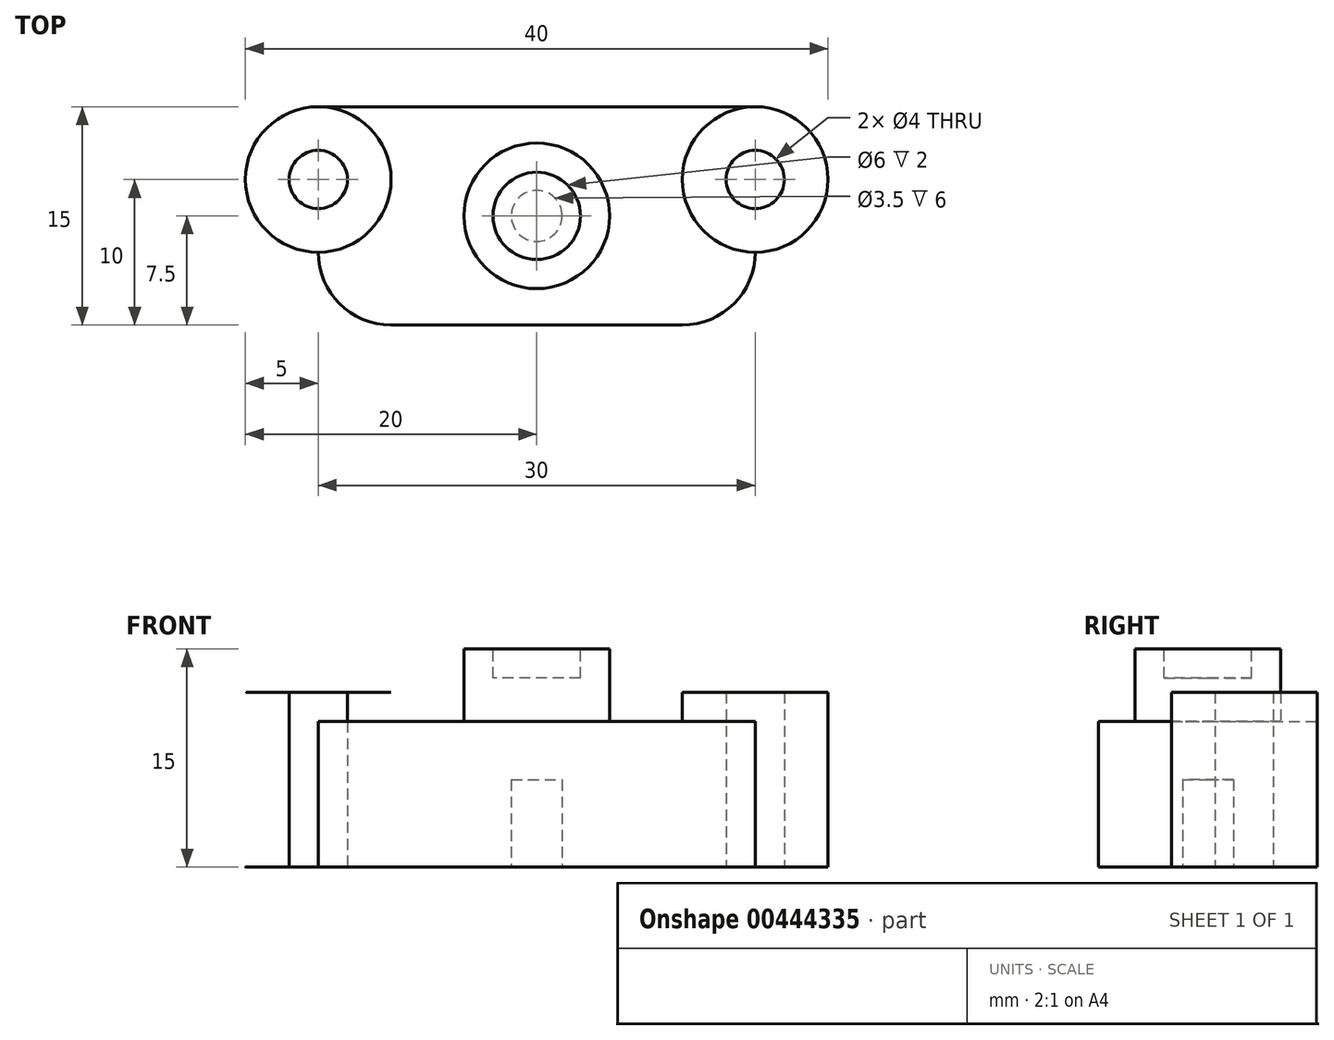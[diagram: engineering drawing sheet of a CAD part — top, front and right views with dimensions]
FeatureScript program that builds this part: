
annotation { "Feature Type Name" : "Feature", "Feature Type Description" : "" }
export const myFeature = defineFeature(function(context is Context, id is Id, definition is map)
    precondition{}
    {
        {
            var Q0;
            Q0=qCreatedBy(makeId("Top.planeOp"),FACE);
            var sketch = newSketch(context, id + "F0", { "sketchPlane" : qUnion([Q0])});
            skLineSegment(sketch, "E0.bottom", {"start": v(10, -7.5) * mm, "end": v(-10, -7.5) * mm});
            skLineSegment(sketch, "E0.top", {"start": v(15, 7.5) * mm, "end": v(-15, 7.5) * mm});
            skLineSegment(sketch, "E0.left", {"start": v(15, -2.5) * mm, "end": v(15, 7.5) * mm});
            skLineSegment(sketch, "E0.right", {"start": v(-15, -2.5) * mm, "end": v(-15, 7.5) * mm});
            skPoint(sketch, "E0.middle", {"position": v(0, 0) * mm});
            skPoint(sketch, "E1.visualSharp", {"position": v(-15, -7.5) * mm});
            skArc(sketch, "E1.filletArc", {"start": v(-15, -2.5) * mm, "mid": v(-13.54, -6.04) * mm, "end": v(-10, -7.5) * mm});
            skPoint(sketch, "E2.visualSharp", {"position": v(15, -7.5) * mm});
            skArc(sketch, "E2.filletArc", {"start": v(10, -7.5) * mm, "mid": v(13.54, -6.04) * mm, "end": v(15, -2.5) * mm});
            skSolve(sketch);
        }
        {
            var Q0;
            Q0=makeQuery(id+"F0.imprint","IMPRINT",FACE,{"disambiguationData":[TD([[makeQuery(id+"F0.imprint","IMPRINT",EDGE,{"derivedFrom":sQuery(id+"F0.wireOp",EDGE,"E0.bottom")}),-1.0]])]});
            extrude(context, id + "F1", {"entities" : qUnion([Q0]), "depth" : 10 * mm});
        }
        {
            var Q0;
            Q0=makeQuery(id+"F1.opExtrude","CAP_FACE",FACE,{"disambiguationData":[OSD([sQuery(id+"F0.wireOp",EDGE,"E0.bottom"),sQuery(id+"F0.wireOp",EDGE,"E0.top"),sQuery(id+"F0.wireOp",EDGE,"E0.left"),sQuery(id+"F0.wireOp",EDGE,"E0.right"),sQuery(id+"F0.wireOp",EDGE,"E1.filletArc"),sQuery(id+"F0.wireOp",EDGE,"E2.filletArc")])],"isStart":false});
            var sketch = newSketch(context, id + "F2", { "sketchPlane" : qUnion([Q0])});
            skCircle(sketch, "E3", {"center": v(0, 0) * mm, "radius": 5 * mm});
            skSolve(sketch);
        }
        {
            var Q0;
            Q0=makeQuery(id+"F2.imprint","IMPRINT",FACE,{"disambiguationData":[TD([[makeQuery(id+"F2.imprint","IMPRINT",EDGE,{"derivedFrom":sQuery(id+"F2.wireOp",EDGE,"E3")}),1.0]])]});
            var Q1;
            Q1=sQuery(id+"F2.wireOp",EDGE,"E3");
            extrude(context, id + "F3", {"entities" : qUnion([Q0]), "operationType" : NewBodyOperationType.ADD, "surfaceEntities" : qUnion([Q1]), "depth" : 5 * mm});
        }
        {
            var Q0;
            Q0=makeQuery(id+"F3.opExtrude","CAP_FACE",FACE,{"disambiguationData":[OSD([sQuery(id+"F2.wireOp",EDGE,"E3")])],"isStart":false});
            var sketch = newSketch(context, id + "F4", { "sketchPlane" : qUnion([Q0])});
            skCircle(sketch, "E4", {"center": v(0, 0) * mm, "radius": 3 * mm});
            skSolve(sketch);
        }
        {
            var Q0;
            Q0 = qSketchRegion(id + "F4", true);
            var Q1;
            Q1=sQuery(id+"F4.wireOp",EDGE,"E4");
            extrude(context, id + "F5", {"entities" : qUnion([Q0]), "operationType" : NewBodyOperationType.REMOVE, "surfaceEntities" : qUnion([Q1]), "oppositeDirection" : true, "depth" : 2 * mm});
        }
        {
            var Q0;
            Q0=makeQuery(id+"F1.opExtrude","CAP_FACE",FACE,{"disambiguationData":[OSD([sQuery(id+"F0.wireOp",EDGE,"E0.bottom"),sQuery(id+"F0.wireOp",EDGE,"E0.top"),sQuery(id+"F0.wireOp",EDGE,"E0.left"),sQuery(id+"F0.wireOp",EDGE,"E0.right"),sQuery(id+"F0.wireOp",EDGE,"E1.filletArc"),sQuery(id+"F0.wireOp",EDGE,"E2.filletArc")])],"isStart":true});
            var sketch = newSketch(context, id + "F6", { "sketchPlane" : qUnion([Q0])});
            skCircle(sketch, "E5", {"center": v(0, 0) * mm, "radius": 1.75 * mm});
            skSolve(sketch);
        }
        {
            var Q0;
            Q0 = qSketchRegion(id + "F6", true);
            extrude(context, id + "F7", {"entities" : qUnion([Q0]), "operationType" : NewBodyOperationType.REMOVE, "oppositeDirection" : true, "depth" : 6 * mm});
        }
        {
            var Q0;
            Q0=qCreatedBy(makeId("Top.planeOp"),FACE);
            var sketch = newSketch(context, id + "F8", { "sketchPlane" : qUnion([Q0])});
            skCircle(sketch, "E6", {"center": v(15, 2.5) * mm, "radius": 5 * mm});
            skSolve(sketch);
        }
        {
            var Q0;
            Q0 = qSketchRegion(id + "F8", true);
            extrude(context, id + "F9", {"entities" : qUnion([Q0]), "operationType" : NewBodyOperationType.ADD, "depth" : 12 * mm});
        }
        {
            var Q0;
            Q0=qCreatedBy(makeId("Top.planeOp"),FACE);
            var sketch = newSketch(context, id + "F10", { "sketchPlane" : qUnion([Q0])});
            skCircle(sketch, "E7", {"center": v(-15, 2.5) * mm, "radius": 5 * mm});
            skSolve(sketch);
        }
        {
            var Q0;
            Q0 = qSketchRegion(id + "F10", true);
            extrude(context, id + "F11", {"entities" : qUnion([Q0]), "operationType" : NewBodyOperationType.ADD, "depth" : 12 * mm});
        }
        {
            var Q0;
            Q0=makeQuery(id+"F11.boolean.opBoolean","MERGE",FACE,{"derivedFrom":[makeQuery(id+"F9.boolean.opBoolean","MERGE",FACE,{"derivedFrom":[makeQuery(id+"F1.opExtrude","CAP_FACE",FACE,{"disambiguationData":[OSD([sQuery(id+"F0.wireOp",EDGE,"E0.bottom"),sQuery(id+"F0.wireOp",EDGE,"E0.top"),sQuery(id+"F0.wireOp",EDGE,"E0.left"),sQuery(id+"F0.wireOp",EDGE,"E0.right"),sQuery(id+"F0.wireOp",EDGE,"E1.filletArc"),sQuery(id+"F0.wireOp",EDGE,"E2.filletArc")])],"isStart":true}),makeQuery(id+"F9.opExtrude","CAP_FACE",FACE,{"disambiguationData":[OSD([sQuery(id+"F8.wireOp",EDGE,"E6")])],"isStart":true})]}),makeQuery(id+"F11.opExtrude","CAP_FACE",FACE,{"disambiguationData":[OSD([sQuery(id+"F10.wireOp",EDGE,"E7")])],"isStart":true})]});
            var sketch = newSketch(context, id + "F12", { "sketchPlane" : qUnion([Q0])});
            skCircle(sketch, "E8", {"center": v(-15, -2.5) * mm, "radius": 2 * mm});
            skSolve(sketch);
        }
        {
            var Q0;
            Q0 = qSketchRegion(id + "F12", true);
            extrude(context, id + "F13", {"entities" : qUnion([Q0]), "operationType" : NewBodyOperationType.REMOVE, "oppositeDirection" : true, "depth" : 12 * mm});
        }
        {
            var Q0;
            Q0=makeQuery(id+"F12.imprint","IMPRINT",FACE,{"disambiguationData":[TD([[makeQuery(id+"F12.imprint","IMPRINT",EDGE,{"derivedFrom":sQuery(id+"F12.wireOp",EDGE,"E8")}),-1.0]])]});
            var sketch = newSketch(context, id + "F14", { "sketchPlane" : qUnion([Q0])});
            skCircle(sketch, "E9", {"center": v(15, -2.5) * mm, "radius": 2 * mm});
            skSolve(sketch);
        }
        {
            var Q0;
            Q0=makeQuery(id+"F14.imprint","IMPRINT",FACE,{"disambiguationData":[TD([[makeQuery(id+"F14.imprint","IMPRINT",EDGE,{"derivedFrom":sQuery(id+"F14.wireOp",EDGE,"E9")}),1.0]])]});
            var Q1;
            Q1=sQuery(id+"F14.wireOp",EDGE,"E9");
            extrude(context, id + "F15", {"entities" : qUnion([Q0]), "operationType" : NewBodyOperationType.REMOVE, "surfaceEntities" : qUnion([Q1]), "endBound" : BoundingType.THROUGH_ALL, "oppositeDirection" : true, "depth" : 10 * mm});
        }
    });
